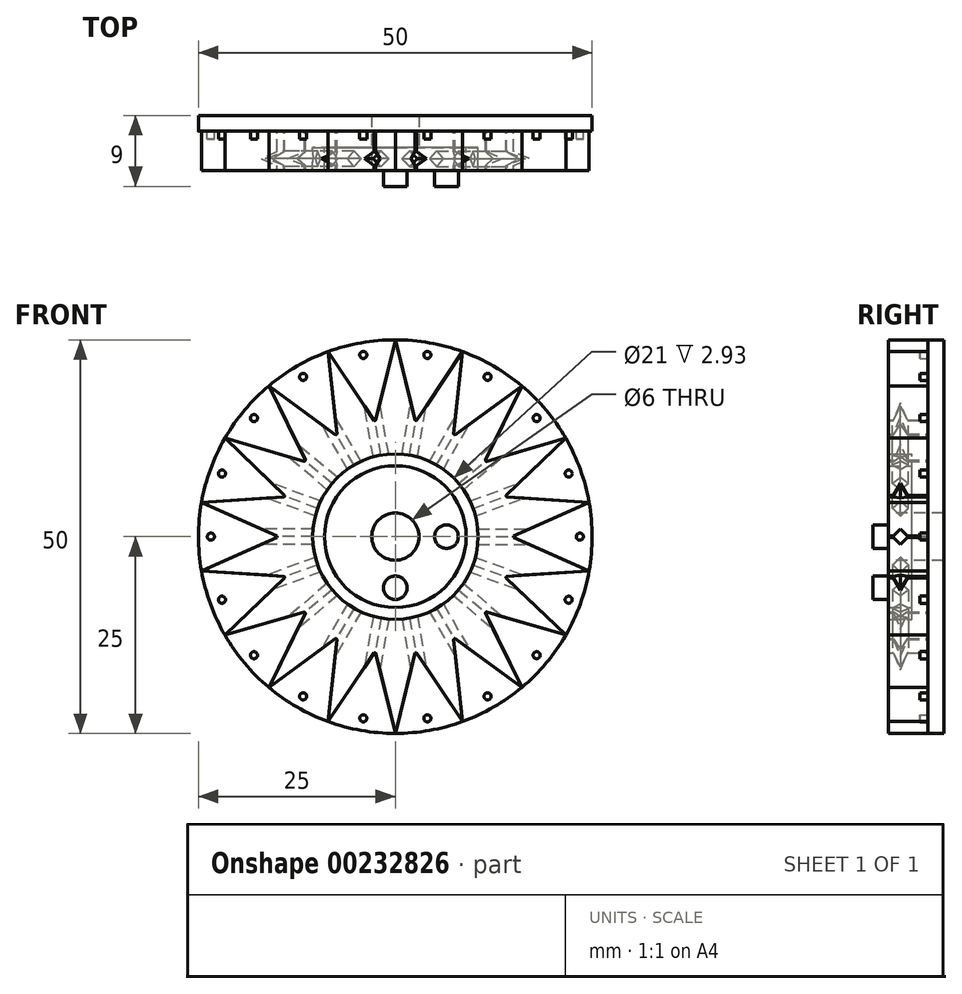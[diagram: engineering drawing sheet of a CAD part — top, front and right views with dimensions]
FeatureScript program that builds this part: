
annotation { "Feature Type Name" : "Feature", "Feature Type Description" : "" }
export const myFeature = defineFeature(function(context is Context, id is Id, definition is map)
    precondition{}
    {
        {
            var Q0;
            Q0=qCreatedBy(makeId("Front.planeOp"),FACE);
            var sketch = newSketch(context, id + "F0", { "sketchPlane" : qUnion([Q0])});
            skCircle(sketch, "E0", {"center": v(0, 0) * mm, "radius": 25 * mm});
            skSolve(sketch);
        }
        {
            var Q0;
            Q0 = qSketchRegion(id + "F0", true);
            extrude(context, id + "F1", {"entities" : qUnion([Q0]), "oppositeDirection" : true, "depth" : 2 * mm, "offsetDistance" : 25 * mm});
        }
        {
            var Q0;
            Q0=qCreatedBy(makeId("Front.planeOp"),FACE);
            var sketch = newSketch(context, id + "F2", { "sketchPlane" : qUnion([Q0])});
            skCircle(sketch, "E1", {"center": v(0, 0) * mm, "radius": 15 * mm});
            skSolve(sketch);
        }
        {
            var Q0;
            Q0 = qSketchRegion(id + "F2", true);
            extrude(context, id + "F3", {"entities" : qUnion([Q0]), "operationType" : NewBodyOperationType.ADD, "depth" : 5 * mm});
        }
        {
            var Q0;
            Q0=qCreatedBy(makeId("Front.planeOp"),FACE);
            var sketch = newSketch(context, id + "F4", { "sketchPlane" : qUnion([Q0])});
            skCircle(sketch, "E2", {"center": v(0, 0) * mm, "radius": 3 * mm});
            skSolve(sketch);
        }
        {
            var Q0;
            Q0 = qSketchRegion(id + "F4", true);
            extrude(context, id + "F5", {"entities" : qUnion([Q0]), "operationType" : NewBodyOperationType.REMOVE, "endBound" : BoundingType.SYMMETRIC, "oppositeDirection" : true, "depth" : 10 * mm});
        }
        {
            var Q0;
            Q0=qCreatedBy(makeId("Front.planeOp"),FACE);
            var sketch = newSketch(context, id + "F6", { "sketchPlane" : qUnion([Q0])});
            skCircle(sketch, "E3", {"center": v(0, 0) * mm, "radius": 15 * mm});
            skCircle(sketch, "E4", {"center": v(0, 0) * mm, "radius": 25 * mm});
            skLineSegment(sketch, "E5", {"start": v(-2.5, 14.8) * mm, "end": v(0, 25) * mm});
            skLineSegment(sketch, "E6", {"start": v(0, 25) * mm, "end": v(0, 25) * mm});
            skLineSegment(sketch, "E7", {"start": v(0, 25) * mm, "end": v(2.5, 14.8) * mm});
            skSolve(sketch);
        }
        {
            var Q0;
            {var subQ0=sQuery(id+"F6.wireOp",EDGE,"E5");Q0=makeQuery(id+"F6.imprint","IMPRINT",FACE,{"disambiguationData":[TD([[makeQuery(id+"F6.imprint","IMPRINT",EDGE,{"derivedFrom":subQ0}),-1.0]])]});}
            extrude(context, id + "F7", {"entities" : qUnion([Q0]), "depth" : 5 * mm});
        }
        {
            var Q0;
            Q0=makeQuery(id+"F7.opExtrude","SWEPT_BODY",BODY,{"disambiguationData":[OSD([sQuery(id+"F6.wireOp",EDGE,"E3"),sQuery(id+"F6.wireOp",EDGE,"E5"),sQuery(id+"F6.wireOp",EDGE,"E7")])]});
            var Q1;
            Q1=sQuery(id+"F4.wireOp",EDGE,"E2");
            transform(context, id + "F8", {"entities" : qUnion([Q0]), "transformType" : TransformType.ROTATION, "transformAxis" : qUnion([Q1]), "angle" : 20 * degree, "oppositeDirection" : true, "makeCopy" : true});
        }
        {
            var Q0;
            Q0=makeQuery(id+"F8.opPattern","COPY",BODY,{"derivedFrom":makeQuery(id+"F7.opExtrude","SWEPT_BODY",BODY,{"disambiguationData":[OSD([sQuery(id+"F6.wireOp",EDGE,"E3"),sQuery(id+"F6.wireOp",EDGE,"E5"),sQuery(id+"F6.wireOp",EDGE,"E7")])]}),"instanceName":"1"});
            var Q1;
            Q1=sQuery(id+"F4.wireOp",EDGE,"E2");
            transform(context, id + "F9", {"entities" : qUnion([Q0]), "transformType" : TransformType.ROTATION, "transformAxis" : qUnion([Q1]), "angle" : 20 * degree, "oppositeDirection" : true, "makeCopy" : true});
        }
        {
            var Q0;
            Q0=makeQuery(id+"F9.opPattern","COPY",BODY,{"derivedFrom":makeQuery(id+"F8.opPattern","COPY",BODY,{"derivedFrom":makeQuery(id+"F7.opExtrude","SWEPT_BODY",BODY,{"disambiguationData":[OSD([sQuery(id+"F6.wireOp",EDGE,"E3"),sQuery(id+"F6.wireOp",EDGE,"E5"),sQuery(id+"F6.wireOp",EDGE,"E7")])]}),"instanceName":"1"}),"instanceName":"1"});
            var Q1;
            Q1=sQuery(id+"F4.wireOp",EDGE,"E2");
            transform(context, id + "F10", {"entities" : qUnion([Q0]), "transformType" : TransformType.ROTATION, "transformAxis" : qUnion([Q1]), "angle" : 20 * degree, "oppositeDirection" : true, "makeCopy" : true});
        }
        {
            var Q0;
            Q0=makeQuery(id+"F10.opPattern","COPY",BODY,{"derivedFrom":makeQuery(id+"F9.opPattern","COPY",BODY,{"derivedFrom":makeQuery(id+"F8.opPattern","COPY",BODY,{"derivedFrom":makeQuery(id+"F7.opExtrude","SWEPT_BODY",BODY,{"disambiguationData":[OSD([sQuery(id+"F6.wireOp",EDGE,"E3"),sQuery(id+"F6.wireOp",EDGE,"E5"),sQuery(id+"F6.wireOp",EDGE,"E7")])]}),"instanceName":"1"}),"instanceName":"1"}),"instanceName":"1"});
            var Q1;
            Q1=sQuery(id+"F4.wireOp",EDGE,"E2");
            transform(context, id + "F11", {"entities" : qUnion([Q0]), "transformType" : TransformType.ROTATION, "transformAxis" : qUnion([Q1]), "angle" : 20 * degree, "oppositeDirection" : true, "makeCopy" : true});
        }
        {
            var Q0;
            Q0=makeQuery(id+"F7.opExtrude","SWEPT_BODY",BODY,{"disambiguationData":[OSD([sQuery(id+"F6.wireOp",EDGE,"E3"),sQuery(id+"F6.wireOp",EDGE,"E5"),sQuery(id+"F6.wireOp",EDGE,"E7")])]});
            var Q1;
            Q1=makeQuery(id+"F8.opPattern","COPY",BODY,{"derivedFrom":makeQuery(id+"F7.opExtrude","SWEPT_BODY",BODY,{"disambiguationData":[OSD([sQuery(id+"F6.wireOp",EDGE,"E3"),sQuery(id+"F6.wireOp",EDGE,"E5"),sQuery(id+"F6.wireOp",EDGE,"E7")])]}),"instanceName":"1"});
            var Q2;
            Q2=makeQuery(id+"F9.opPattern","COPY",BODY,{"derivedFrom":makeQuery(id+"F8.opPattern","COPY",BODY,{"derivedFrom":makeQuery(id+"F7.opExtrude","SWEPT_BODY",BODY,{"disambiguationData":[OSD([sQuery(id+"F6.wireOp",EDGE,"E3"),sQuery(id+"F6.wireOp",EDGE,"E5"),sQuery(id+"F6.wireOp",EDGE,"E7")])]}),"instanceName":"1"}),"instanceName":"1"});
            var Q3;
            Q3=makeQuery(id+"F10.opPattern","COPY",BODY,{"derivedFrom":makeQuery(id+"F9.opPattern","COPY",BODY,{"derivedFrom":makeQuery(id+"F8.opPattern","COPY",BODY,{"derivedFrom":makeQuery(id+"F7.opExtrude","SWEPT_BODY",BODY,{"disambiguationData":[OSD([sQuery(id+"F6.wireOp",EDGE,"E3"),sQuery(id+"F6.wireOp",EDGE,"E5"),sQuery(id+"F6.wireOp",EDGE,"E7")])]}),"instanceName":"1"}),"instanceName":"1"}),"instanceName":"1"});
            var Q4;
            Q4=makeQuery(id+"F11.opPattern","COPY",BODY,{"derivedFrom":makeQuery(id+"F10.opPattern","COPY",BODY,{"derivedFrom":makeQuery(id+"F9.opPattern","COPY",BODY,{"derivedFrom":makeQuery(id+"F8.opPattern","COPY",BODY,{"derivedFrom":makeQuery(id+"F7.opExtrude","SWEPT_BODY",BODY,{"disambiguationData":[OSD([sQuery(id+"F6.wireOp",EDGE,"E3"),sQuery(id+"F6.wireOp",EDGE,"E5"),sQuery(id+"F6.wireOp",EDGE,"E7")])]}),"instanceName":"1"}),"instanceName":"1"}),"instanceName":"1"}),"instanceName":"1"});
            var Q5;
            Q5=qCreatedBy(makeId("Right.planeOp"),FACE);
            mirror(context, id + "F12", {"entities" : qUnion([Q0, Q1, Q2, Q3, Q4]), "mirrorPlane" : qUnion([Q5])});
        }
        {
            var Q0;
            Q0=makeQuery(id+"F12.opPattern","COPY",BODY,{"derivedFrom":makeQuery(id+"F11.opPattern","COPY",BODY,{"derivedFrom":makeQuery(id+"F10.opPattern","COPY",BODY,{"derivedFrom":makeQuery(id+"F9.opPattern","COPY",BODY,{"derivedFrom":makeQuery(id+"F8.opPattern","COPY",BODY,{"derivedFrom":makeQuery(id+"F7.opExtrude","SWEPT_BODY",BODY,{"disambiguationData":[OSD([sQuery(id+"F6.wireOp",EDGE,"E3"),sQuery(id+"F6.wireOp",EDGE,"E5"),sQuery(id+"F6.wireOp",EDGE,"E7")])]}),"instanceName":"1"}),"instanceName":"1"}),"instanceName":"1"}),"instanceName":"1"}),"instanceName":"1"});
            var Q1;
            Q1=makeQuery(id+"F12.opPattern","COPY",BODY,{"derivedFrom":makeQuery(id+"F10.opPattern","COPY",BODY,{"derivedFrom":makeQuery(id+"F9.opPattern","COPY",BODY,{"derivedFrom":makeQuery(id+"F8.opPattern","COPY",BODY,{"derivedFrom":makeQuery(id+"F7.opExtrude","SWEPT_BODY",BODY,{"disambiguationData":[OSD([sQuery(id+"F6.wireOp",EDGE,"E3"),sQuery(id+"F6.wireOp",EDGE,"E5"),sQuery(id+"F6.wireOp",EDGE,"E7")])]}),"instanceName":"1"}),"instanceName":"1"}),"instanceName":"1"}),"instanceName":"1"});
            var Q2;
            Q2=makeQuery(id+"F12.opPattern","COPY",BODY,{"derivedFrom":makeQuery(id+"F9.opPattern","COPY",BODY,{"derivedFrom":makeQuery(id+"F8.opPattern","COPY",BODY,{"derivedFrom":makeQuery(id+"F7.opExtrude","SWEPT_BODY",BODY,{"disambiguationData":[OSD([sQuery(id+"F6.wireOp",EDGE,"E3"),sQuery(id+"F6.wireOp",EDGE,"E5"),sQuery(id+"F6.wireOp",EDGE,"E7")])]}),"instanceName":"1"}),"instanceName":"1"}),"instanceName":"1"});
            var Q3;
            Q3=makeQuery(id+"F12.opPattern","COPY",BODY,{"derivedFrom":makeQuery(id+"F8.opPattern","COPY",BODY,{"derivedFrom":makeQuery(id+"F7.opExtrude","SWEPT_BODY",BODY,{"disambiguationData":[OSD([sQuery(id+"F6.wireOp",EDGE,"E3"),sQuery(id+"F6.wireOp",EDGE,"E5"),sQuery(id+"F6.wireOp",EDGE,"E7")])]}),"instanceName":"1"}),"instanceName":"1"});
            var Q4;
            Q4=makeQuery(id+"F12.opPattern","COPY",BODY,{"derivedFrom":makeQuery(id+"F7.opExtrude","SWEPT_BODY",BODY,{"disambiguationData":[OSD([sQuery(id+"F6.wireOp",EDGE,"E3"),sQuery(id+"F6.wireOp",EDGE,"E5"),sQuery(id+"F6.wireOp",EDGE,"E7")])]}),"instanceName":"1"});
            var Q5;
            Q5=makeQuery(id+"F8.opPattern","COPY",BODY,{"derivedFrom":makeQuery(id+"F7.opExtrude","SWEPT_BODY",BODY,{"disambiguationData":[OSD([sQuery(id+"F6.wireOp",EDGE,"E3"),sQuery(id+"F6.wireOp",EDGE,"E5"),sQuery(id+"F6.wireOp",EDGE,"E7")])]}),"instanceName":"1"});
            var Q6;
            Q6=makeQuery(id+"F9.opPattern","COPY",BODY,{"derivedFrom":makeQuery(id+"F8.opPattern","COPY",BODY,{"derivedFrom":makeQuery(id+"F7.opExtrude","SWEPT_BODY",BODY,{"disambiguationData":[OSD([sQuery(id+"F6.wireOp",EDGE,"E3"),sQuery(id+"F6.wireOp",EDGE,"E5"),sQuery(id+"F6.wireOp",EDGE,"E7")])]}),"instanceName":"1"}),"instanceName":"1"});
            var Q7;
            Q7=makeQuery(id+"F10.opPattern","COPY",BODY,{"derivedFrom":makeQuery(id+"F9.opPattern","COPY",BODY,{"derivedFrom":makeQuery(id+"F8.opPattern","COPY",BODY,{"derivedFrom":makeQuery(id+"F7.opExtrude","SWEPT_BODY",BODY,{"disambiguationData":[OSD([sQuery(id+"F6.wireOp",EDGE,"E3"),sQuery(id+"F6.wireOp",EDGE,"E5"),sQuery(id+"F6.wireOp",EDGE,"E7")])]}),"instanceName":"1"}),"instanceName":"1"}),"instanceName":"1"});
            var Q8;
            Q8=makeQuery(id+"F11.opPattern","COPY",BODY,{"derivedFrom":makeQuery(id+"F10.opPattern","COPY",BODY,{"derivedFrom":makeQuery(id+"F9.opPattern","COPY",BODY,{"derivedFrom":makeQuery(id+"F8.opPattern","COPY",BODY,{"derivedFrom":makeQuery(id+"F7.opExtrude","SWEPT_BODY",BODY,{"disambiguationData":[OSD([sQuery(id+"F6.wireOp",EDGE,"E3"),sQuery(id+"F6.wireOp",EDGE,"E5"),sQuery(id+"F6.wireOp",EDGE,"E7")])]}),"instanceName":"1"}),"instanceName":"1"}),"instanceName":"1"}),"instanceName":"1"});
            var Q9;
            Q9=qCreatedBy(makeId("Top.planeOp"),FACE);
            mirror(context, id + "F13", {"operationType" : NewBodyOperationType.ADD, "entities" : qUnion([Q0, Q1, Q2, Q3, Q4, Q5, Q6, Q7, Q8]), "mirrorPlane" : qUnion([Q9])});
        }
        {
            var Q0;
            Q0=makeQuery(id+"F6.imprint","IMPRINT",FACE,{"disambiguationData":[TD([[makeQuery(id+"F6.imprint","IMPRINT",EDGE,{"derivedFrom":sQuery(id+"F6.wireOp",EDGE,"E4")}),1.0]])]});
            var sketch = newSketch(context, id + "F14", { "sketchPlane" : qUnion([Q0])});
            skPoint(sketch, "E8", {"position": v(4.07, 23.08) * mm});
            skCircle(sketch, "E9", {"center": v(4.07, 23.08) * mm, "radius": 0.45 * mm});
            skSolve(sketch);
        }
        {
            var Q0;
            Q0 = qSketchRegion(id + "F14", true);
            extrude(context, id + "F15", {"entities" : qUnion([Q0]), "depth" : 1 * mm});
        }
        {
            var Q0;
            Q0=makeQuery(id+"F15.opExtrude","SWEPT_BODY",BODY,{"disambiguationData":[OSD([sQuery(id+"F14.wireOp",EDGE,"E9")])]});
            var Q1;
            Q1=sQuery(id+"F4.wireOp",EDGE,"E2");
            transform(context, id + "F16", {"entities" : qUnion([Q0]), "transformType" : TransformType.ROTATION, "transformAxis" : qUnion([Q1]), "angle" : 20 * degree, "makeCopy" : true});
        }
        {
            var Q0;
            Q0=makeQuery(id+"F16.opPattern","COPY",BODY,{"derivedFrom":makeQuery(id+"F15.opExtrude","SWEPT_BODY",BODY,{"disambiguationData":[OSD([sQuery(id+"F14.wireOp",EDGE,"E9")])]}),"instanceName":"1"});
            var Q1;
            Q1=sQuery(id+"F4.wireOp",EDGE,"E2");
            transform(context, id + "F17", {"entities" : qUnion([Q0]), "transformType" : TransformType.ROTATION, "transformAxis" : qUnion([Q1]), "angle" : 20 * degree, "makeCopy" : true});
        }
        {
            var Q0;
            Q0=makeQuery(id+"F17.opPattern","COPY",BODY,{"derivedFrom":makeQuery(id+"F16.opPattern","COPY",BODY,{"derivedFrom":makeQuery(id+"F15.opExtrude","SWEPT_BODY",BODY,{"disambiguationData":[OSD([sQuery(id+"F14.wireOp",EDGE,"E9")])]}),"instanceName":"1"}),"instanceName":"1"});
            var Q1;
            Q1=sQuery(id+"F4.wireOp",EDGE,"E2");
            transform(context, id + "F18", {"entities" : qUnion([Q0]), "transformType" : TransformType.ROTATION, "transformAxis" : qUnion([Q1]), "angle" : 20 * degree, "makeCopy" : true});
        }
        {
            var Q0;
            Q0=makeQuery(id+"F18.opPattern","COPY",BODY,{"derivedFrom":makeQuery(id+"F17.opPattern","COPY",BODY,{"derivedFrom":makeQuery(id+"F16.opPattern","COPY",BODY,{"derivedFrom":makeQuery(id+"F15.opExtrude","SWEPT_BODY",BODY,{"disambiguationData":[OSD([sQuery(id+"F14.wireOp",EDGE,"E9")])]}),"instanceName":"1"}),"instanceName":"1"}),"instanceName":"1"});
            var Q1;
            Q1=sQuery(id+"F4.wireOp",EDGE,"E2");
            transform(context, id + "F19", {"entities" : qUnion([Q0]), "transformType" : TransformType.ROTATION, "transformAxis" : qUnion([Q1]), "angle" : 20 * degree, "makeCopy" : true});
        }
        {
            var Q0;
            Q0=makeQuery(id+"F19.opPattern","COPY",BODY,{"derivedFrom":makeQuery(id+"F18.opPattern","COPY",BODY,{"derivedFrom":makeQuery(id+"F17.opPattern","COPY",BODY,{"derivedFrom":makeQuery(id+"F16.opPattern","COPY",BODY,{"derivedFrom":makeQuery(id+"F15.opExtrude","SWEPT_BODY",BODY,{"disambiguationData":[OSD([sQuery(id+"F14.wireOp",EDGE,"E9")])]}),"instanceName":"1"}),"instanceName":"1"}),"instanceName":"1"}),"instanceName":"1"});
            var Q1;
            Q1=sQuery(id+"F4.wireOp",EDGE,"E2");
            transform(context, id + "F20", {"entities" : qUnion([Q0]), "transformType" : TransformType.ROTATION, "transformAxis" : qUnion([Q1]), "angle" : 20 * degree, "makeCopy" : true});
        }
        {
            var Q0;
            Q0=makeQuery(id+"F19.opPattern","COPY",BODY,{"derivedFrom":makeQuery(id+"F18.opPattern","COPY",BODY,{"derivedFrom":makeQuery(id+"F17.opPattern","COPY",BODY,{"derivedFrom":makeQuery(id+"F16.opPattern","COPY",BODY,{"derivedFrom":makeQuery(id+"F15.opExtrude","SWEPT_BODY",BODY,{"disambiguationData":[OSD([sQuery(id+"F14.wireOp",EDGE,"E9")])]}),"instanceName":"1"}),"instanceName":"1"}),"instanceName":"1"}),"instanceName":"1"});
            var Q1;
            Q1=makeQuery(id+"F18.opPattern","COPY",BODY,{"derivedFrom":makeQuery(id+"F17.opPattern","COPY",BODY,{"derivedFrom":makeQuery(id+"F16.opPattern","COPY",BODY,{"derivedFrom":makeQuery(id+"F15.opExtrude","SWEPT_BODY",BODY,{"disambiguationData":[OSD([sQuery(id+"F14.wireOp",EDGE,"E9")])]}),"instanceName":"1"}),"instanceName":"1"}),"instanceName":"1"});
            var Q2;
            Q2=makeQuery(id+"F17.opPattern","COPY",BODY,{"derivedFrom":makeQuery(id+"F16.opPattern","COPY",BODY,{"derivedFrom":makeQuery(id+"F15.opExtrude","SWEPT_BODY",BODY,{"disambiguationData":[OSD([sQuery(id+"F14.wireOp",EDGE,"E9")])]}),"instanceName":"1"}),"instanceName":"1"});
            var Q3;
            Q3=makeQuery(id+"F16.opPattern","COPY",BODY,{"derivedFrom":makeQuery(id+"F15.opExtrude","SWEPT_BODY",BODY,{"disambiguationData":[OSD([sQuery(id+"F14.wireOp",EDGE,"E9")])]}),"instanceName":"1"});
            var Q4;
            Q4=qCreatedBy(makeId("Top.planeOp"),FACE);
            mirror(context, id + "F21", {"entities" : qUnion([Q0, Q1, Q2, Q3]), "mirrorPlane" : qUnion([Q4])});
        }
        {
            var Q0;
            Q0=makeQuery(id+"F21.opPattern","COPY",BODY,{"derivedFrom":makeQuery(id+"F16.opPattern","COPY",BODY,{"derivedFrom":makeQuery(id+"F15.opExtrude","SWEPT_BODY",BODY,{"disambiguationData":[OSD([sQuery(id+"F14.wireOp",EDGE,"E9")])]}),"instanceName":"1"}),"instanceName":"1"});
            var Q1;
            Q1=makeQuery(id+"F21.opPattern","COPY",BODY,{"derivedFrom":makeQuery(id+"F17.opPattern","COPY",BODY,{"derivedFrom":makeQuery(id+"F16.opPattern","COPY",BODY,{"derivedFrom":makeQuery(id+"F15.opExtrude","SWEPT_BODY",BODY,{"disambiguationData":[OSD([sQuery(id+"F14.wireOp",EDGE,"E9")])]}),"instanceName":"1"}),"instanceName":"1"}),"instanceName":"1"});
            var Q2;
            Q2=makeQuery(id+"F21.opPattern","COPY",BODY,{"derivedFrom":makeQuery(id+"F18.opPattern","COPY",BODY,{"derivedFrom":makeQuery(id+"F17.opPattern","COPY",BODY,{"derivedFrom":makeQuery(id+"F16.opPattern","COPY",BODY,{"derivedFrom":makeQuery(id+"F15.opExtrude","SWEPT_BODY",BODY,{"disambiguationData":[OSD([sQuery(id+"F14.wireOp",EDGE,"E9")])]}),"instanceName":"1"}),"instanceName":"1"}),"instanceName":"1"}),"instanceName":"1"});
            var Q3;
            Q3=makeQuery(id+"F21.opPattern","COPY",BODY,{"derivedFrom":makeQuery(id+"F19.opPattern","COPY",BODY,{"derivedFrom":makeQuery(id+"F18.opPattern","COPY",BODY,{"derivedFrom":makeQuery(id+"F17.opPattern","COPY",BODY,{"derivedFrom":makeQuery(id+"F16.opPattern","COPY",BODY,{"derivedFrom":makeQuery(id+"F15.opExtrude","SWEPT_BODY",BODY,{"disambiguationData":[OSD([sQuery(id+"F14.wireOp",EDGE,"E9")])]}),"instanceName":"1"}),"instanceName":"1"}),"instanceName":"1"}),"instanceName":"1"}),"instanceName":"1"});
            var Q4;
            Q4=makeQuery(id+"F20.opPattern","COPY",BODY,{"derivedFrom":makeQuery(id+"F19.opPattern","COPY",BODY,{"derivedFrom":makeQuery(id+"F18.opPattern","COPY",BODY,{"derivedFrom":makeQuery(id+"F17.opPattern","COPY",BODY,{"derivedFrom":makeQuery(id+"F16.opPattern","COPY",BODY,{"derivedFrom":makeQuery(id+"F15.opExtrude","SWEPT_BODY",BODY,{"disambiguationData":[OSD([sQuery(id+"F14.wireOp",EDGE,"E9")])]}),"instanceName":"1"}),"instanceName":"1"}),"instanceName":"1"}),"instanceName":"1"}),"instanceName":"1"});
            var Q5;
            Q5=makeQuery(id+"F19.opPattern","COPY",BODY,{"derivedFrom":makeQuery(id+"F18.opPattern","COPY",BODY,{"derivedFrom":makeQuery(id+"F17.opPattern","COPY",BODY,{"derivedFrom":makeQuery(id+"F16.opPattern","COPY",BODY,{"derivedFrom":makeQuery(id+"F15.opExtrude","SWEPT_BODY",BODY,{"disambiguationData":[OSD([sQuery(id+"F14.wireOp",EDGE,"E9")])]}),"instanceName":"1"}),"instanceName":"1"}),"instanceName":"1"}),"instanceName":"1"});
            var Q6;
            Q6=makeQuery(id+"F18.opPattern","COPY",BODY,{"derivedFrom":makeQuery(id+"F17.opPattern","COPY",BODY,{"derivedFrom":makeQuery(id+"F16.opPattern","COPY",BODY,{"derivedFrom":makeQuery(id+"F15.opExtrude","SWEPT_BODY",BODY,{"disambiguationData":[OSD([sQuery(id+"F14.wireOp",EDGE,"E9")])]}),"instanceName":"1"}),"instanceName":"1"}),"instanceName":"1"});
            var Q7;
            Q7=makeQuery(id+"F17.opPattern","COPY",BODY,{"derivedFrom":makeQuery(id+"F16.opPattern","COPY",BODY,{"derivedFrom":makeQuery(id+"F15.opExtrude","SWEPT_BODY",BODY,{"disambiguationData":[OSD([sQuery(id+"F14.wireOp",EDGE,"E9")])]}),"instanceName":"1"}),"instanceName":"1"});
            var Q8;
            Q8=qCreatedBy(makeId("Right.planeOp"),FACE);
            mirror(context, id + "F22", {"operationType" : NewBodyOperationType.ADD, "entities" : qUnion([Q0, Q1, Q2, Q3, Q4, Q5, Q6, Q7]), "mirrorPlane" : qUnion([Q8])});
        }
        {
            var Q0;
            Q0=qCreatedBy(makeId("Front.planeOp"),FACE);
            var sketch = newSketch(context, id + "F23", { "sketchPlane" : qUnion([Q0])});
            skCircle(sketch, "E10", {"center": v(0, 0) * mm, "radius": 10.5 * mm});
            skCircle(sketch, "E11", {"center": v(0, 0) * mm, "radius": 9 * mm});
            skSolve(sketch);
        }
        {
            var Q0;
            Q0 = qSketchRegion(id + "F23", true);
            extrude(context, id + "F24", {"entities" : qUnion([Q0]), "depth" : 3 * mm});
        }
        {
            var Q0;
            Q0=makeQuery(id+"F24.opExtrude","SWEPT_BODY",BODY,{"disambiguationData":[OSD([sQuery(id+"F23.wireOp",EDGE,"E10"),sQuery(id+"F23.wireOp",EDGE,"E11")])]});
            transform(context, id + "F25", {"entities" : qUnion([Q0]), "transformType" : TransformType.TRANSLATION_3D, "dx" : 0 * mm, "dy" : -2.07 * mm, "dz" : 0 * mm, "makeCopy" : false});
        }
        {
            var Q0;
            Q0=makeQuery(id+"F24.opExtrude","SWEPT_BODY",BODY,{"disambiguationData":[OSD([sQuery(id+"F23.wireOp",EDGE,"E10"),sQuery(id+"F23.wireOp",EDGE,"E11")])]});
            var Q1;
            Q1=makeQuery(id+"F1.opExtrude","SWEPT_BODY",BODY,{"disambiguationData":[OSD([sQuery(id+"F0.wireOp",EDGE,"E0")])]});
            booleanBodies(context, id + "F26", {"operationType" : BooleanOperationType.SUBTRACTION, "tools" : qUnion([Q0]), "targets" : qUnion([Q1])});
        }
        {
            var Q0;
            Q0=qCreatedBy(makeId("Top.planeOp"),FACE);
            var sketch = newSketch(context, id + "F27", { "sketchPlane" : qUnion([Q0])});
            skCircle(sketch, "E12.cCircle", {"center": v(0, -2.6) * mm, "radius": 1 * mm, "construction": true});
            skLineSegment(sketch, "E12.0", {"start": v(1, -2.6) * mm, "end": v(0, -3.6) * mm});
            skLineSegment(sketch, "E12.1", {"start": v(0, -3.6) * mm, "end": v(-1, -2.6) * mm});
            skLineSegment(sketch, "E12.2", {"start": v(-1, -2.6) * mm, "end": v(0, -1.6) * mm});
            skLineSegment(sketch, "E12.3", {"start": v(0, -1.6) * mm, "end": v(1, -2.6) * mm});
            skSolve(sketch);
        }
        {
            var Q0;
            Q0=makeQuery(id+"F27.imprint","IMPRINT",FACE,{"disambiguationData":[TD([[makeQuery(id+"F27.imprint","IMPRINT",EDGE,{"derivedFrom":sQuery(id+"F27.wireOp",EDGE,"E12.0")}),-1.0]])]});
            var Q1;
            Q1=sQuery(id+"F27.wireOp",EDGE,"E12.2");
            var Q2;
            Q2=sQuery(id+"F27.wireOp",EDGE,"E12.3");
            var Q3;
            Q3=sQuery(id+"F27.wireOp",EDGE,"E12.0");
            var Q4;
            Q4=sQuery(id+"F27.wireOp",EDGE,"E12.1");
            extrude(context, id + "F28", {"entities" : qUnion([Q0]), "surfaceEntities" : qUnion([Q1, Q2, Q3, Q4]), "endBound" : BoundingType.SYMMETRIC, "oppositeDirection" : true, "depth" : 10 * mm});
        }
        {
            var Q0;
            Q0=makeQuery(id+"F28.opExtrude","SWEPT_BODY",BODY,{"disambiguationData":[OSD([sQuery(id+"F27.wireOp",EDGE,"E12.0"),sQuery(id+"F27.wireOp",EDGE,"E12.1"),sQuery(id+"F27.wireOp",EDGE,"E12.2"),sQuery(id+"F27.wireOp",EDGE,"E12.3")])]});
            transform(context, id + "F29", {"entities" : qUnion([Q0]), "transformType" : TransformType.TRANSLATION_3D, "dx" : 0 * mm, "dy" : -0.9 * mm, "dz" : 15 * mm, "makeCopy" : false});
        }
        {
            var Q0;
            Q0=makeQuery(id+"F28.opExtrude","SWEPT_BODY",BODY,{"disambiguationData":[OSD([sQuery(id+"F27.wireOp",EDGE,"E12.0"),sQuery(id+"F27.wireOp",EDGE,"E12.1"),sQuery(id+"F27.wireOp",EDGE,"E12.2"),sQuery(id+"F27.wireOp",EDGE,"E12.3")])]});
            var Q1;
            Q1=sQuery(id+"F4.wireOp",EDGE,"E2");
            transform(context, id + "F30", {"entities" : qUnion([Q0]), "transformType" : TransformType.ROTATION, "transformAxis" : qUnion([Q1]), "angle" : 10 * degree, "makeCopy" : false});
        }
        {
            var Q0;
            Q0=makeQuery(id+"F28.opExtrude","SWEPT_BODY",BODY,{"disambiguationData":[OSD([sQuery(id+"F27.wireOp",EDGE,"E12.0"),sQuery(id+"F27.wireOp",EDGE,"E12.1"),sQuery(id+"F27.wireOp",EDGE,"E12.2"),sQuery(id+"F27.wireOp",EDGE,"E12.3")])]});
            var Q1;
            Q1=sQuery(id+"F4.wireOp",EDGE,"E2");
            transform(context, id + "F31", {"entities" : qUnion([Q0]), "transformType" : TransformType.ROTATION, "transformAxis" : qUnion([Q1]), "angle" : 20 * degree, "makeCopy" : true});
        }
        {
            var Q0;
            Q0=makeQuery(id+"F31.opPattern","COPY",BODY,{"derivedFrom":makeQuery(id+"F28.opExtrude","SWEPT_BODY",BODY,{"disambiguationData":[OSD([sQuery(id+"F27.wireOp",EDGE,"E12.0"),sQuery(id+"F27.wireOp",EDGE,"E12.1"),sQuery(id+"F27.wireOp",EDGE,"E12.2"),sQuery(id+"F27.wireOp",EDGE,"E12.3")])]}),"instanceName":"1"});
            var Q1;
            Q1=sQuery(id+"F4.wireOp",EDGE,"E2");
            transform(context, id + "F32", {"entities" : qUnion([Q0]), "transformType" : TransformType.ROTATION, "transformAxis" : qUnion([Q1]), "angle" : 20 * degree, "makeCopy" : true});
        }
        {
            var Q0;
            Q0=makeQuery(id+"F32.opPattern","COPY",BODY,{"derivedFrom":makeQuery(id+"F31.opPattern","COPY",BODY,{"derivedFrom":makeQuery(id+"F28.opExtrude","SWEPT_BODY",BODY,{"disambiguationData":[OSD([sQuery(id+"F27.wireOp",EDGE,"E12.0"),sQuery(id+"F27.wireOp",EDGE,"E12.1"),sQuery(id+"F27.wireOp",EDGE,"E12.2"),sQuery(id+"F27.wireOp",EDGE,"E12.3")])]}),"instanceName":"1"}),"instanceName":"1"});
            var Q1;
            Q1=sQuery(id+"F4.wireOp",EDGE,"E2");
            transform(context, id + "F33", {"entities" : qUnion([Q0]), "transformType" : TransformType.ROTATION, "transformAxis" : qUnion([Q1]), "angle" : 20 * degree, "makeCopy" : true});
        }
        {
            var Q0;
            Q0=makeQuery(id+"F33.opPattern","COPY",BODY,{"derivedFrom":makeQuery(id+"F32.opPattern","COPY",BODY,{"derivedFrom":makeQuery(id+"F31.opPattern","COPY",BODY,{"derivedFrom":makeQuery(id+"F28.opExtrude","SWEPT_BODY",BODY,{"disambiguationData":[OSD([sQuery(id+"F27.wireOp",EDGE,"E12.0"),sQuery(id+"F27.wireOp",EDGE,"E12.1"),sQuery(id+"F27.wireOp",EDGE,"E12.2"),sQuery(id+"F27.wireOp",EDGE,"E12.3")])]}),"instanceName":"1"}),"instanceName":"1"}),"instanceName":"1"});
            var Q1;
            Q1=sQuery(id+"F4.wireOp",EDGE,"E2");
            transform(context, id + "F34", {"entities" : qUnion([Q0]), "transformType" : TransformType.ROTATION, "transformAxis" : qUnion([Q1]), "angle" : 20 * degree, "makeCopy" : true});
        }
        {
            var Q0;
            Q0=makeQuery(id+"F28.opExtrude","SWEPT_BODY",BODY,{"disambiguationData":[OSD([sQuery(id+"F27.wireOp",EDGE,"E12.0"),sQuery(id+"F27.wireOp",EDGE,"E12.1"),sQuery(id+"F27.wireOp",EDGE,"E12.2"),sQuery(id+"F27.wireOp",EDGE,"E12.3")])]});
            var Q1;
            Q1=makeQuery(id+"F31.opPattern","COPY",BODY,{"derivedFrom":makeQuery(id+"F28.opExtrude","SWEPT_BODY",BODY,{"disambiguationData":[OSD([sQuery(id+"F27.wireOp",EDGE,"E12.0"),sQuery(id+"F27.wireOp",EDGE,"E12.1"),sQuery(id+"F27.wireOp",EDGE,"E12.2"),sQuery(id+"F27.wireOp",EDGE,"E12.3")])]}),"instanceName":"1"});
            var Q2;
            Q2=makeQuery(id+"F32.opPattern","COPY",BODY,{"derivedFrom":makeQuery(id+"F31.opPattern","COPY",BODY,{"derivedFrom":makeQuery(id+"F28.opExtrude","SWEPT_BODY",BODY,{"disambiguationData":[OSD([sQuery(id+"F27.wireOp",EDGE,"E12.0"),sQuery(id+"F27.wireOp",EDGE,"E12.1"),sQuery(id+"F27.wireOp",EDGE,"E12.2"),sQuery(id+"F27.wireOp",EDGE,"E12.3")])]}),"instanceName":"1"}),"instanceName":"1"});
            var Q3;
            Q3=makeQuery(id+"F33.opPattern","COPY",BODY,{"derivedFrom":makeQuery(id+"F32.opPattern","COPY",BODY,{"derivedFrom":makeQuery(id+"F31.opPattern","COPY",BODY,{"derivedFrom":makeQuery(id+"F28.opExtrude","SWEPT_BODY",BODY,{"disambiguationData":[OSD([sQuery(id+"F27.wireOp",EDGE,"E12.0"),sQuery(id+"F27.wireOp",EDGE,"E12.1"),sQuery(id+"F27.wireOp",EDGE,"E12.2"),sQuery(id+"F27.wireOp",EDGE,"E12.3")])]}),"instanceName":"1"}),"instanceName":"1"}),"instanceName":"1"});
            var Q4;
            Q4=qCreatedBy(makeId("Top.planeOp"),FACE);
            mirror(context, id + "F35", {"entities" : qUnion([Q0, Q1, Q2, Q3]), "mirrorPlane" : qUnion([Q4])});
        }
        {
            var Q0;
            Q0=makeQuery(id+"F28.opExtrude","SWEPT_BODY",BODY,{"disambiguationData":[OSD([sQuery(id+"F27.wireOp",EDGE,"E12.0"),sQuery(id+"F27.wireOp",EDGE,"E12.1"),sQuery(id+"F27.wireOp",EDGE,"E12.2"),sQuery(id+"F27.wireOp",EDGE,"E12.3")])]});
            var Q1;
            Q1=makeQuery(id+"F31.opPattern","COPY",BODY,{"derivedFrom":makeQuery(id+"F28.opExtrude","SWEPT_BODY",BODY,{"disambiguationData":[OSD([sQuery(id+"F27.wireOp",EDGE,"E12.0"),sQuery(id+"F27.wireOp",EDGE,"E12.1"),sQuery(id+"F27.wireOp",EDGE,"E12.2"),sQuery(id+"F27.wireOp",EDGE,"E12.3")])]}),"instanceName":"1"});
            var Q2;
            Q2=makeQuery(id+"F32.opPattern","COPY",BODY,{"derivedFrom":makeQuery(id+"F31.opPattern","COPY",BODY,{"derivedFrom":makeQuery(id+"F28.opExtrude","SWEPT_BODY",BODY,{"disambiguationData":[OSD([sQuery(id+"F27.wireOp",EDGE,"E12.0"),sQuery(id+"F27.wireOp",EDGE,"E12.1"),sQuery(id+"F27.wireOp",EDGE,"E12.2"),sQuery(id+"F27.wireOp",EDGE,"E12.3")])]}),"instanceName":"1"}),"instanceName":"1"});
            var Q3;
            Q3=makeQuery(id+"F35.opPattern","COPY",BODY,{"derivedFrom":makeQuery(id+"F32.opPattern","COPY",BODY,{"derivedFrom":makeQuery(id+"F31.opPattern","COPY",BODY,{"derivedFrom":makeQuery(id+"F28.opExtrude","SWEPT_BODY",BODY,{"disambiguationData":[OSD([sQuery(id+"F27.wireOp",EDGE,"E12.0"),sQuery(id+"F27.wireOp",EDGE,"E12.1"),sQuery(id+"F27.wireOp",EDGE,"E12.2"),sQuery(id+"F27.wireOp",EDGE,"E12.3")])]}),"instanceName":"1"}),"instanceName":"1"}),"instanceName":"1"});
            var Q4;
            Q4=makeQuery(id+"F35.opPattern","COPY",BODY,{"derivedFrom":makeQuery(id+"F31.opPattern","COPY",BODY,{"derivedFrom":makeQuery(id+"F28.opExtrude","SWEPT_BODY",BODY,{"disambiguationData":[OSD([sQuery(id+"F27.wireOp",EDGE,"E12.0"),sQuery(id+"F27.wireOp",EDGE,"E12.1"),sQuery(id+"F27.wireOp",EDGE,"E12.2"),sQuery(id+"F27.wireOp",EDGE,"E12.3")])]}),"instanceName":"1"}),"instanceName":"1"});
            var Q5;
            Q5=makeQuery(id+"F35.opPattern","COPY",BODY,{"derivedFrom":makeQuery(id+"F28.opExtrude","SWEPT_BODY",BODY,{"disambiguationData":[OSD([sQuery(id+"F27.wireOp",EDGE,"E12.0"),sQuery(id+"F27.wireOp",EDGE,"E12.1"),sQuery(id+"F27.wireOp",EDGE,"E12.2"),sQuery(id+"F27.wireOp",EDGE,"E12.3")])]}),"instanceName":"1"});
            var Q6;
            Q6=makeQuery(id+"F33.opPattern","COPY",BODY,{"derivedFrom":makeQuery(id+"F32.opPattern","COPY",BODY,{"derivedFrom":makeQuery(id+"F31.opPattern","COPY",BODY,{"derivedFrom":makeQuery(id+"F28.opExtrude","SWEPT_BODY",BODY,{"disambiguationData":[OSD([sQuery(id+"F27.wireOp",EDGE,"E12.0"),sQuery(id+"F27.wireOp",EDGE,"E12.1"),sQuery(id+"F27.wireOp",EDGE,"E12.2"),sQuery(id+"F27.wireOp",EDGE,"E12.3")])]}),"instanceName":"1"}),"instanceName":"1"}),"instanceName":"1"});
            var Q7;
            Q7=makeQuery(id+"F34.opPattern","COPY",BODY,{"derivedFrom":makeQuery(id+"F33.opPattern","COPY",BODY,{"derivedFrom":makeQuery(id+"F32.opPattern","COPY",BODY,{"derivedFrom":makeQuery(id+"F31.opPattern","COPY",BODY,{"derivedFrom":makeQuery(id+"F28.opExtrude","SWEPT_BODY",BODY,{"disambiguationData":[OSD([sQuery(id+"F27.wireOp",EDGE,"E12.0"),sQuery(id+"F27.wireOp",EDGE,"E12.1"),sQuery(id+"F27.wireOp",EDGE,"E12.2"),sQuery(id+"F27.wireOp",EDGE,"E12.3")])]}),"instanceName":"1"}),"instanceName":"1"}),"instanceName":"1"}),"instanceName":"1"});
            var Q8;
            Q8=makeQuery(id+"F35.opPattern","COPY",BODY,{"derivedFrom":makeQuery(id+"F33.opPattern","COPY",BODY,{"derivedFrom":makeQuery(id+"F32.opPattern","COPY",BODY,{"derivedFrom":makeQuery(id+"F31.opPattern","COPY",BODY,{"derivedFrom":makeQuery(id+"F28.opExtrude","SWEPT_BODY",BODY,{"disambiguationData":[OSD([sQuery(id+"F27.wireOp",EDGE,"E12.0"),sQuery(id+"F27.wireOp",EDGE,"E12.1"),sQuery(id+"F27.wireOp",EDGE,"E12.2"),sQuery(id+"F27.wireOp",EDGE,"E12.3")])]}),"instanceName":"1"}),"instanceName":"1"}),"instanceName":"1"}),"instanceName":"1"});
            var Q9;
            Q9=qCreatedBy(makeId("Right.planeOp"),FACE);
            mirror(context, id + "F36", {"operationType" : NewBodyOperationType.REMOVE, "entities" : qUnion([Q0, Q1, Q2, Q3, Q4, Q5, Q6, Q7, Q8]), "mirrorPlane" : qUnion([Q9])});
        }
        {
            var Q0;
            Q0=makeQuery(id+"F28.opExtrude","SWEPT_BODY",BODY,{"disambiguationData":[OSD([sQuery(id+"F27.wireOp",EDGE,"E12.0"),sQuery(id+"F27.wireOp",EDGE,"E12.1"),sQuery(id+"F27.wireOp",EDGE,"E12.2"),sQuery(id+"F27.wireOp",EDGE,"E12.3")])]});
            var Q1;
            Q1=makeQuery(id+"F31.opPattern","COPY",BODY,{"derivedFrom":makeQuery(id+"F28.opExtrude","SWEPT_BODY",BODY,{"disambiguationData":[OSD([sQuery(id+"F27.wireOp",EDGE,"E12.0"),sQuery(id+"F27.wireOp",EDGE,"E12.1"),sQuery(id+"F27.wireOp",EDGE,"E12.2"),sQuery(id+"F27.wireOp",EDGE,"E12.3")])]}),"instanceName":"1"});
            var Q2;
            Q2=makeQuery(id+"F32.opPattern","COPY",BODY,{"derivedFrom":makeQuery(id+"F31.opPattern","COPY",BODY,{"derivedFrom":makeQuery(id+"F28.opExtrude","SWEPT_BODY",BODY,{"disambiguationData":[OSD([sQuery(id+"F27.wireOp",EDGE,"E12.0"),sQuery(id+"F27.wireOp",EDGE,"E12.1"),sQuery(id+"F27.wireOp",EDGE,"E12.2"),sQuery(id+"F27.wireOp",EDGE,"E12.3")])]}),"instanceName":"1"}),"instanceName":"1"});
            var Q3;
            Q3=makeQuery(id+"F33.opPattern","COPY",BODY,{"derivedFrom":makeQuery(id+"F32.opPattern","COPY",BODY,{"derivedFrom":makeQuery(id+"F31.opPattern","COPY",BODY,{"derivedFrom":makeQuery(id+"F28.opExtrude","SWEPT_BODY",BODY,{"disambiguationData":[OSD([sQuery(id+"F27.wireOp",EDGE,"E12.0"),sQuery(id+"F27.wireOp",EDGE,"E12.1"),sQuery(id+"F27.wireOp",EDGE,"E12.2"),sQuery(id+"F27.wireOp",EDGE,"E12.3")])]}),"instanceName":"1"}),"instanceName":"1"}),"instanceName":"1"});
            var Q4;
            Q4=makeQuery(id+"F35.opPattern","COPY",BODY,{"derivedFrom":makeQuery(id+"F33.opPattern","COPY",BODY,{"derivedFrom":makeQuery(id+"F32.opPattern","COPY",BODY,{"derivedFrom":makeQuery(id+"F31.opPattern","COPY",BODY,{"derivedFrom":makeQuery(id+"F28.opExtrude","SWEPT_BODY",BODY,{"disambiguationData":[OSD([sQuery(id+"F27.wireOp",EDGE,"E12.0"),sQuery(id+"F27.wireOp",EDGE,"E12.1"),sQuery(id+"F27.wireOp",EDGE,"E12.2"),sQuery(id+"F27.wireOp",EDGE,"E12.3")])]}),"instanceName":"1"}),"instanceName":"1"}),"instanceName":"1"}),"instanceName":"1"});
            var Q5;
            Q5=makeQuery(id+"F35.opPattern","COPY",BODY,{"derivedFrom":makeQuery(id+"F32.opPattern","COPY",BODY,{"derivedFrom":makeQuery(id+"F31.opPattern","COPY",BODY,{"derivedFrom":makeQuery(id+"F28.opExtrude","SWEPT_BODY",BODY,{"disambiguationData":[OSD([sQuery(id+"F27.wireOp",EDGE,"E12.0"),sQuery(id+"F27.wireOp",EDGE,"E12.1"),sQuery(id+"F27.wireOp",EDGE,"E12.2"),sQuery(id+"F27.wireOp",EDGE,"E12.3")])]}),"instanceName":"1"}),"instanceName":"1"}),"instanceName":"1"});
            var Q6;
            Q6=makeQuery(id+"F35.opPattern","COPY",BODY,{"derivedFrom":makeQuery(id+"F31.opPattern","COPY",BODY,{"derivedFrom":makeQuery(id+"F28.opExtrude","SWEPT_BODY",BODY,{"disambiguationData":[OSD([sQuery(id+"F27.wireOp",EDGE,"E12.0"),sQuery(id+"F27.wireOp",EDGE,"E12.1"),sQuery(id+"F27.wireOp",EDGE,"E12.2"),sQuery(id+"F27.wireOp",EDGE,"E12.3")])]}),"instanceName":"1"}),"instanceName":"1"});
            var Q7;
            Q7=makeQuery(id+"F35.opPattern","COPY",BODY,{"derivedFrom":makeQuery(id+"F28.opExtrude","SWEPT_BODY",BODY,{"disambiguationData":[OSD([sQuery(id+"F27.wireOp",EDGE,"E12.0"),sQuery(id+"F27.wireOp",EDGE,"E12.1"),sQuery(id+"F27.wireOp",EDGE,"E12.2"),sQuery(id+"F27.wireOp",EDGE,"E12.3")])]}),"instanceName":"1"});
            var Q8;
            Q8=makeQuery(id+"F34.opPattern","COPY",BODY,{"derivedFrom":makeQuery(id+"F33.opPattern","COPY",BODY,{"derivedFrom":makeQuery(id+"F32.opPattern","COPY",BODY,{"derivedFrom":makeQuery(id+"F31.opPattern","COPY",BODY,{"derivedFrom":makeQuery(id+"F28.opExtrude","SWEPT_BODY",BODY,{"disambiguationData":[OSD([sQuery(id+"F27.wireOp",EDGE,"E12.0"),sQuery(id+"F27.wireOp",EDGE,"E12.1"),sQuery(id+"F27.wireOp",EDGE,"E12.2"),sQuery(id+"F27.wireOp",EDGE,"E12.3")])]}),"instanceName":"1"}),"instanceName":"1"}),"instanceName":"1"}),"instanceName":"1"});
            var Q9;
            Q9=makeQuery(id+"F1.opExtrude","SWEPT_BODY",BODY,{"disambiguationData":[OSD([sQuery(id+"F0.wireOp",EDGE,"E0")])]});
            booleanBodies(context, id + "F37", {"operationType" : BooleanOperationType.SUBTRACTION, "tools" : qUnion([Q0, Q1, Q2, Q3, Q4, Q5, Q6, Q7, Q8]), "targets" : qUnion([Q9])});
        }
        {
            var Q0;
            {var subQ0=sQuery(id+"F6.wireOp",EDGE,"E5");var subQ12=sQuery(id+"F6.wireOp",EDGE,"E7");var subQ18=sQuery(id+"F2.wireOp",EDGE,"E1");var subQ37=makeQuery(id+"F7.opExtrude","CAP_FACE",FACE,{"disambiguationData":[OSD([sQuery(id+"F6.wireOp",EDGE,"E3"),subQ0,subQ12])],"isStart":false});var subQ38=makeQuery(id+"F8.opPattern","COPY",FACE,{"derivedFrom":subQ37,"instanceName":"1"});var subQ39=makeQuery(id+"F9.opPattern","COPY",FACE,{"derivedFrom":subQ38,"instanceName":"1"});var subQ40=makeQuery(id+"F10.opPattern","COPY",FACE,{"derivedFrom":subQ39,"instanceName":"1"});var subQ41=makeQuery(id+"F11.opPattern","COPY",FACE,{"derivedFrom":subQ40,"instanceName":"1"});var subQ42=makeQuery(id+"FJje8SWJFmpt1fg_2.opPattern","COPY",FACE,{"derivedFrom":subQ41,"instanceName":"1"});var subQ43=makeQuery(id+"FNIreFu6lhATYbJ_2.opPattern","COPY",FACE,{"derivedFrom":subQ42,"instanceName":"1"});var subQ44=makeQuery(id+"F1Hu8rJiOVGrj8X_2.opPattern","COPY",FACE,{"derivedFrom":subQ43,"instanceName":"1"});var subQ45=makeQuery(id+"FKlUNtfDpntRQfv_2.opPattern","COPY",FACE,{"derivedFrom":subQ44,"instanceName":"1"});var subQ46=makeQuery(id+"FipGwqvm4DIIxyn_2.opPattern","COPY",FACE,{"derivedFrom":subQ45,"instanceName":"1"});var subQ47=makeQuery(id+"FdWrJyMEZw8qYC4_2.opPattern","COPY",FACE,{"derivedFrom":subQ46,"instanceName":"1"});var subQ48=makeQuery(id+"FRqrqO2ZcdNCrlz_2.opPattern","COPY",FACE,{"derivedFrom":subQ47,"instanceName":"1"});var subQ49=makeQuery(id+"FxZ1NIeM0RTfYao_2.opPattern","COPY",FACE,{"derivedFrom":subQ48,"instanceName":"1"});var subQ50=makeQuery(id+"FqIYFQ0VqZavCJ2_2.opPattern","COPY",FACE,{"derivedFrom":subQ49,"instanceName":"1"});var subQ51=makeQuery(id+"FrCz7EWV2lXSKxY_2.opPattern","COPY",FACE,{"derivedFrom":subQ50,"instanceName":"1"});var subQ52=makeQuery(id+"F2Y0soQxFTmYcnx_2.opPattern","COPY",FACE,{"derivedFrom":subQ51,"instanceName":"1"});var subQ53=makeQuery(id+"FeI8slN2iZCsX0w_2.opPattern","COPY",FACE,{"derivedFrom":subQ52,"instanceName":"1"});Q0=makeQuery(id+"F26.opBoolean","SPLIT",FACE,{"disambiguationData":[TD([makeQuery(id+"F3.opExtrude","SWEPT_FACE",FACE,{"disambiguationData":[OSD([subQ18])]})])],"derivedFrom":makeQuery(id+"Fs8PK0LG18piLvF_3.opBoolean","MERGE",FACE,{"derivedFrom":[makeQuery(id+"F3.opExtrude","CAP_FACE",FACE,{"disambiguationData":[OSD([subQ18])],"isStart":false}),subQ37,subQ38,subQ39,subQ40,subQ41,subQ42,subQ43,subQ44,subQ45,subQ46,subQ47,subQ48,subQ49,subQ50,subQ51,subQ52,subQ53,makeQuery(id+"FsVOc05rhOXhNKD_2.opPattern","COPY",FACE,{"derivedFrom":subQ53,"instanceName":"1"})]})});}
            var sketch = newSketch(context, id + "F38", { "sketchPlane" : qUnion([Q0])});
            skCircle(sketch, "E13", {"center": v(0, -6.5) * mm, "radius": 1.5 * mm});
            skCircle(sketch, "E14", {"center": v(6.5, 0) * mm, "radius": 1.5 * mm});
            skSolve(sketch);
        }
        {
            var Q0;
            Q0=makeQuery(id+"F38.imprint","IMPRINT",FACE,{"disambiguationData":[TD([[makeQuery(id+"F38.imprint","IMPRINT",EDGE,{"derivedFrom":sQuery(id+"F38.wireOp",EDGE,"E14")}),1.0]])]});
            var Q1;
            Q1=makeQuery(id+"F38.imprint","IMPRINT",FACE,{"disambiguationData":[TD([[makeQuery(id+"F38.imprint","IMPRINT",EDGE,{"derivedFrom":sQuery(id+"F38.wireOp",EDGE,"E13")}),1.0]])]});
            var Q2;
            Q2=sQuery(id+"F38.wireOp",EDGE,"E14");
            var Q3;
            Q3=sQuery(id+"F38.wireOp",EDGE,"E13");
            extrude(context, id + "F39", {"entities" : qUnion([Q0, Q1]), "operationType" : NewBodyOperationType.ADD, "surfaceEntities" : qUnion([Q2, Q3]), "depth" : 2 * mm});
        }
    });
